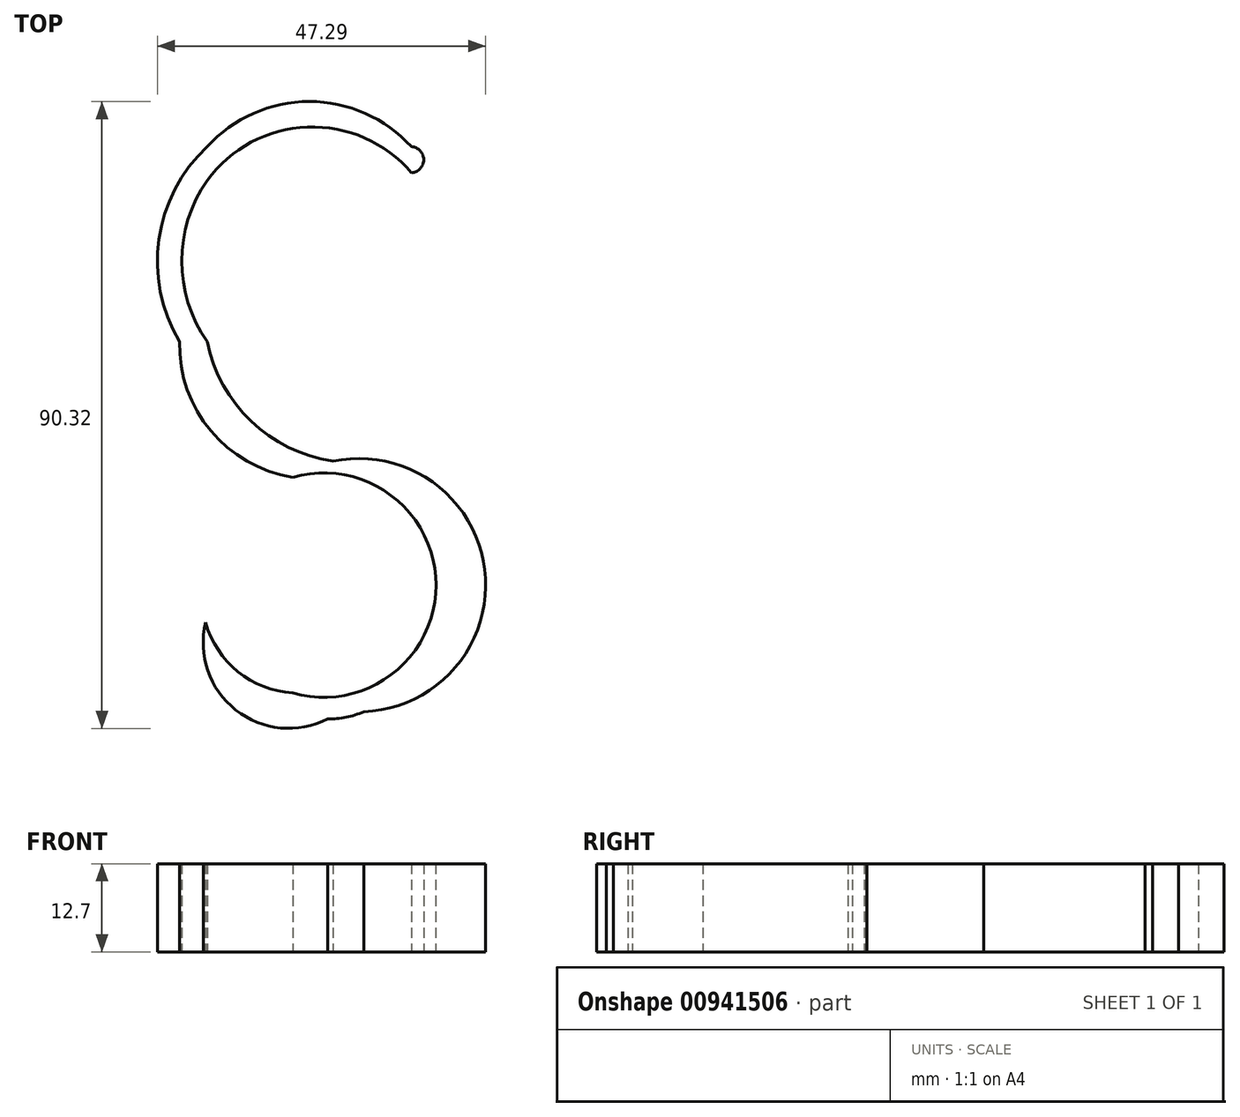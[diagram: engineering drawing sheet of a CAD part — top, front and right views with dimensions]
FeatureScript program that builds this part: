
annotation { "Feature Type Name" : "Feature", "Feature Type Description" : "" }
export const myFeature = defineFeature(function(context is Context, id is Id, definition is map)
    precondition{}
    {
        {
            var Q0;
            Q0=qCreatedBy(makeId("Top.planeOp"),FACE);
            var sketch = newSketch(context, id + "F0", { "sketchPlane" : qUnion([Q0])});
            skArc(sketch, "E0", {"start": v(0, -31.1) * mm, "mid": v(20.62, -15.55) * mm, "end": v(0, 0) * mm});
            skArc(sketch, "E1", {"start": v(-12.55, -20.92) * mm, "mid": v(-7.9, -28.01) * mm, "end": v(0, -31.1) * mm});
            skArc(sketch, "E2", {"start": v(0, -31.1) * mm, "mid": v(27.79, -15.55) * mm, "end": v(0, 0) * mm});
            skArc(sketch, "E3", {"start": v(-12.55, -20.92) * mm, "mid": v(-7.3, -34.2) * mm, "end": v(6.97, -33.6) * mm});
            skArc(sketch, "E4", {"start": v(0, -33.6) * mm, "mid": v(7.4, -34.65) * mm, "end": v(13.99, -31.1) * mm});
            skArc(sketch, "E5", {"start": v(-16.3, 19.55) * mm, "mid": v(-11.82, 6.71) * mm, "end": v(0, 0) * mm});
            skArc(sketch, "E6", {"start": v(-12.33, 47.63) * mm, "mid": v(-19.28, 34.3) * mm, "end": v(-16.3, 19.55) * mm});
            skArc(sketch, "E7", {"start": v(17.08, 47.63) * mm, "mid": v(2.38, 54.13) * mm, "end": v(-12.33, 47.63) * mm});
            skArc(sketch, "E8", {"start": v(17.08, 43.87) * mm, "mid": v(2.11, 50.46) * mm, "end": v(-12.33, 42.77) * mm});
            skArc(sketch, "E9", {"start": v(-12.33, 42.77) * mm, "mid": v(-15.99, 31.16) * mm, "end": v(-12.33, 19.55) * mm});
            skArc(sketch, "E10", {"start": v(-12.33, 19.55) * mm, "mid": v(-3.23, 5.84) * mm, "end": v(12.85, 2.4) * mm});
            skArc(sketch, "E11", {"start": v(17.08, 43.87) * mm, "mid": v(18.86, 45.75) * mm, "end": v(17.08, 47.63) * mm});
            skSolve(sketch);
        }
        {
            var Q0;
            Q0 = qSketchRegion(id + "F0", true);
            extrude(context, id + "F1", {"entities" : qUnion([Q0]), "depth" : 12.7 * mm, "offsetDistance" : 25.4 * mm});
        }
    });
